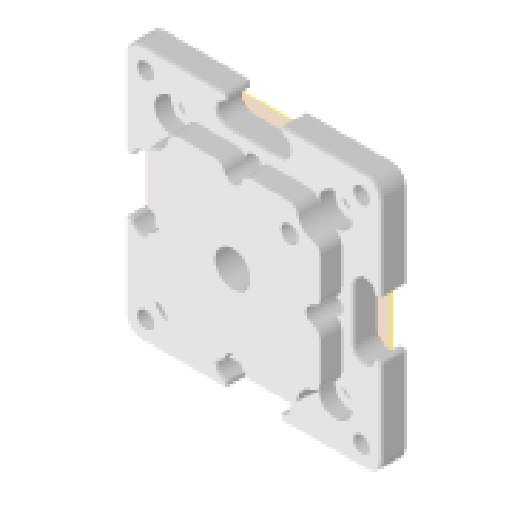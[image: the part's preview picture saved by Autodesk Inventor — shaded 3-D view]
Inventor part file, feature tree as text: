
AUTODESK INVENTOR PART (.ipt)
format: ipt  version: 2024.1 (Build 281209000, 209)  size: 608,256 bytes
history: native  units: mm
features: reference x11, extrude x4, other x3, sketch x2, plane x1, hole x1, pattern_circular x1, chamfer x1, fillet x1, projected_geometry x1
ambient origin geometry x8: Origin, YZ Plane, XZ Plane, XY Plane, X Axis, Y Axis, Z Axis, Center Point
bodies: Volumenkörper1 (feature_tree)
feature tree (26):
  plane  "Arbeitsebene1"
  extrude  "Extrusion1"  Depth=49.8mm
  extrude  "Extrusion2"  Depth=42.0mm
  hole  "Bohrung1"  [1 undecoded]
  extrude  "Extrusion3"  Depth=3.2mm
  pattern_circular  "Runde Anordnung1"  [2 undecoded]
  chamfer  "Fase1"  Distance=3.2mm
  extrude  "Extrusion4"  Depth=5.0mm TaperAngle=0.0deg
  fillet  "Rundung1"  Radius=5.4mm
  reference  "Referenz1"
  sketch  "Skizze2"  dims[d0=49.8mm d1=49.8mm]
  sketch  "Skizze4"  dims[d2=3.0mm d3=42.0mm d4=42.0mm d5=3.2mm d7=3.2mm d8=3.2mm d9=5.0mm d10=0.0mm d11=5.4mm d12=5.4mm d13=5.4mm d14=5.4mm d15=2.6mm d16=0.0mm d17=3.2mm d18=6.0mm d19=6.5mm d20=3.0mm d21=90.0deg d22=8.0mm d23=20.594885mm d24=0.1mm d25=0.0mm d26=0.0mm d27=40.0mm d28=360.0deg d30=0.3mm d31=2.0mm d32=45.0deg d33=3.2mm d34=34.4mm d35=34.4mm d36=4.0mm d37=-0.523599mm d38=2.0mm]
  reference  "Referenz2"
  reference  "Referenz3"
  reference  "Referenz4"
  reference  "Referenz5"
  reference  "Referenz6"
  reference  "Referenz7"
  reference  "Referenz8"
  reference  "Referenz9"
  reference  "Referenz10"
  reference  "Referenz11"
  projected_geometry  "Projizierte Kontur1"
  other  "Assembly_XYZ_Stage_Micrometer_ontop.iam"
  other  "00_XYZstage_micro_LT-4047-S1:1"
  other  "10_Base_puzzle_v3:1"
note: 3 required parameter values undecoded (feature->parameter linkage not recoverable at this tier; creation-order binding heuristic only, values carry confidence <= 0.55)
